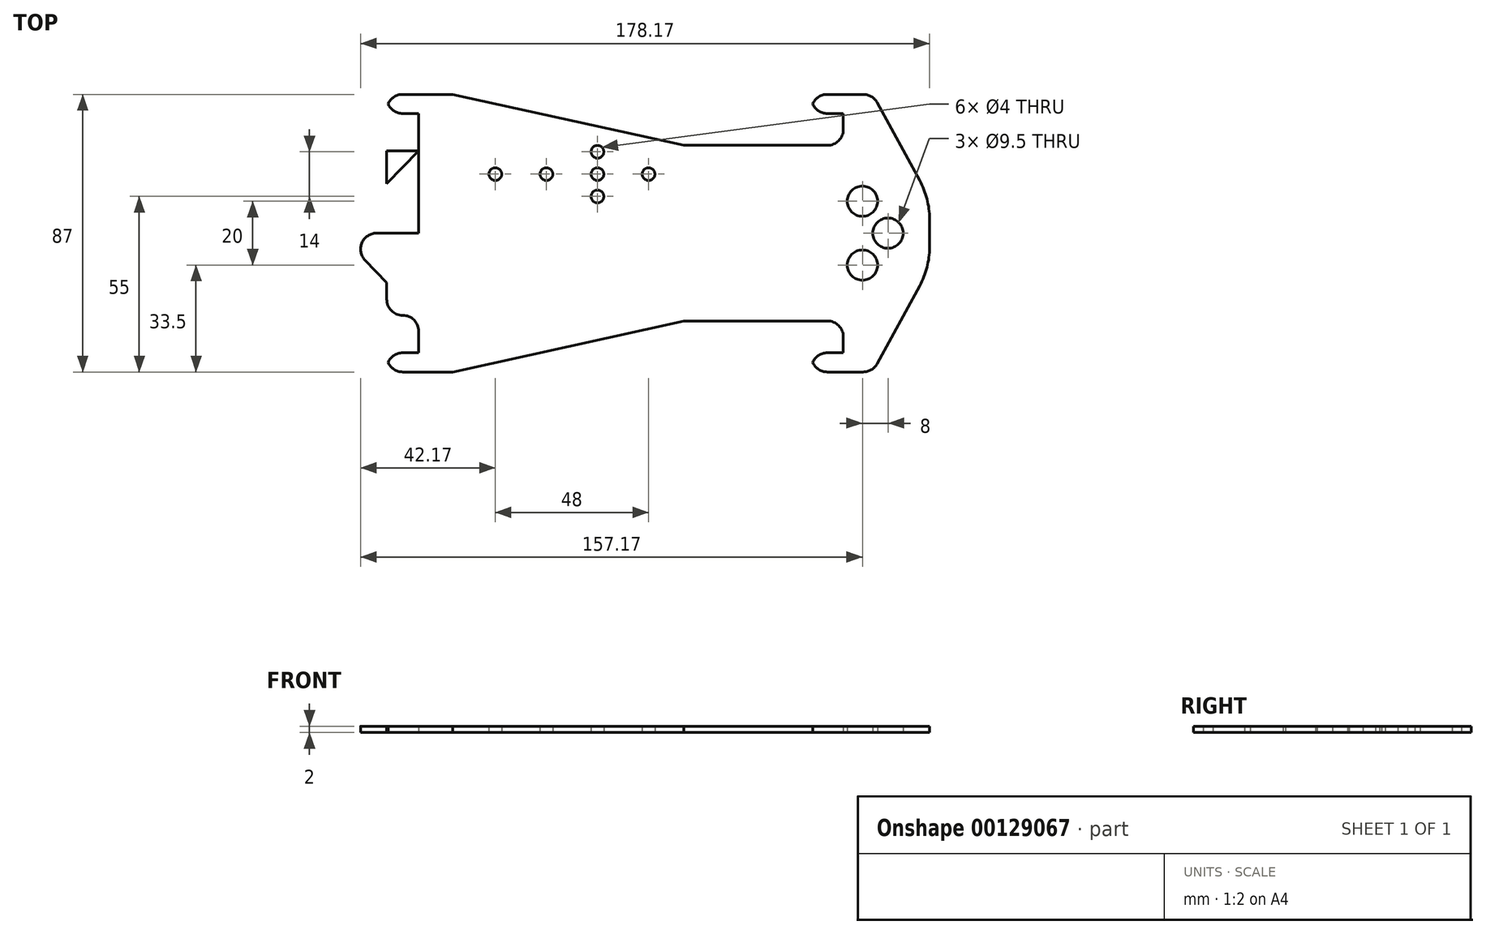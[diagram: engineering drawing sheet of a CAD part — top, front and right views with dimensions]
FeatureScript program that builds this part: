
annotation { "Feature Type Name" : "Feature", "Feature Type Description" : "" }
export const myFeature = defineFeature(function(context is Context, id is Id, definition is map)
    precondition{}
    {
        {
            var Q0;
            Q0=qCreatedBy(makeId("Top.planeOp"),FACE);
            var sketch = newSketch(context, id + "F0", { "sketchPlane" : qUnion([Q0])});
            skLineSegment(sketch, "E0.bottom", {"start": v(85, -43.5) * mm, "end": v(-85, -43.5) * mm});
            skLineSegment(sketch, "E0.top", {"start": v(85, 43.5) * mm, "end": v(-85, 43.5) * mm});
            skLineSegment(sketch, "E0.left", {"start": v(85, -43.5) * mm, "end": v(85, 43.5) * mm});
            skLineSegment(sketch, "E0.right", {"start": v(-85, -43.5) * mm, "end": v(-85, 43.5) * mm});
            skPoint(sketch, "E0.middle", {"position": v(0, 0) * mm});
            skLineSegment(sketch, "E1", {"start": v(-85, -37.5) * mm, "end": v(-75, -37.5) * mm});
            skLineSegment(sketch, "E2", {"start": v(-75, -37.5) * mm, "end": v(-75, 0) * mm});
            skLineSegment(sketch, "E3.MirrorCS", {"start": v(-75, 37.5) * mm, "end": v(-75, 0) * mm});
            skLineSegment(sketch, "E4.MirrorCS", {"start": v(-85, 37.5) * mm, "end": v(-75, 37.5) * mm});
            skLineSegment(sketch, "E5", {"start": v(48, -43.5) * mm, "end": v(48, -37.5) * mm});
            skLineSegment(sketch, "E6", {"start": v(48, -37.5) * mm, "end": v(58, -37.5) * mm});
            skLineSegment(sketch, "E7", {"start": v(58, -37.5) * mm, "end": v(58, -27.5) * mm});
            skLineSegment(sketch, "E8", {"start": v(58, -27.5) * mm, "end": v(8, -27.5) * mm});
            skLineSegment(sketch, "E9", {"start": v(8, -27.5) * mm, "end": v(-64.29, -43.5) * mm});
            skLineSegment(sketch, "E10.MirrorCS", {"start": v(8, 27.5) * mm, "end": v(-64.29, 43.5) * mm});
            skLineSegment(sketch, "E11.MirrorCS", {"start": v(58, 27.5) * mm, "end": v(8, 27.5) * mm});
            skLineSegment(sketch, "E12.MirrorCS", {"start": v(58, 37.5) * mm, "end": v(58, 27.5) * mm});
            skLineSegment(sketch, "E13.MirrorCS", {"start": v(48, 37.5) * mm, "end": v(58, 37.5) * mm});
            skLineSegment(sketch, "E14.MirrorCS", {"start": v(48, 43.5) * mm, "end": v(48, 37.5) * mm});
            skLineSegment(sketch, "E15", {"start": v(67.19, -43.5) * mm, "end": v(85, -10.86) * mm});
            skLineSegment(sketch, "E16.MirrorCS", {"start": v(67.19, 43.5) * mm, "end": v(85, 10.86) * mm});
            skCircle(sketch, "E17", {"center": v(-3, 18.5) * mm, "radius": 2 * mm});
            skCircle(sketch, "E18", {"center": v(-35, 18.5) * mm, "radius": 2 * mm});
            skCircle(sketch, "E19", {"center": v(-19, 11.5) * mm, "radius": 2 * mm});
            skCircle(sketch, "E20", {"center": v(-19, 25.5) * mm, "radius": 2 * mm});
            skCircle(sketch, "E21", {"center": v(-51, 18.5) * mm, "radius": 2 * mm});
            skLineSegment(sketch, "E22", {"start": v(-75, 25.74) * mm, "end": v(-100, 25.74) * mm});
            skLineSegment(sketch, "E23", {"start": v(-100, 25.74) * mm, "end": v(-100, 0) * mm});
            skLineSegment(sketch, "E24", {"start": v(-100, 0) * mm, "end": v(-75, 0) * mm});
            skLineSegment(sketch, "E25.MirrorCS", {"start": v(-75, -25.74) * mm, "end": v(-100, -25.74) * mm});
            skLineSegment(sketch, "E26.MirrorCS", {"start": v(-100, -25.74) * mm, "end": v(-100, 0) * mm});
            skCircle(sketch, "E27", {"center": v(72, 0) * mm, "radius": 4.75 * mm});
            skCircle(sketch, "E28", {"center": v(64, -10) * mm, "radius": 4.75 * mm});
            skCircle(sketch, "E29.MirrorC", {"center": v(64, 10) * mm, "radius": 4.75 * mm});
            skCircle(sketch, "E30", {"center": v(-19, 18.5) * mm, "radius": 2 * mm});
            skCircle(sketch, "E31", {"center": v(-87.5, 0) * mm, "radius": 4.75 * mm});
            skLineSegment(sketch, "E32", {"start": v(-75, 25.74) * mm, "end": v(-100, 0) * mm});
            skLineSegment(sketch, "E33", {"start": v(-75, -25.74) * mm, "end": v(-100, 0) * mm});
            skSolve(sketch);
        }
        {
            var Q0;
            {var subQ8=sQuery(id+"F0.wireOp",EDGE,"E1");Q0=makeQuery(id+"F0.imprint","IMPRINT",FACE,{"disambiguationData":[TD([[makeQuery(id+"F0.imprint","IMPRINT",EDGE,{"derivedFrom":subQ8}),-1.0]])]});}
            var Q1;
            {var subQ0=sQuery(id+"F0.wireOp",EDGE,"E31");var subQ1=sQuery(id+"F0.wireOp",EDGE,"E0.right");var subQ2=makeQuery(id+"F0.imprint","INTERSECT",VERTEX,{"disambiguationData":[OD(1.0)],"derivedFrom":[subQ1,subQ0]});Q1=makeQuery(id+"F0.imprint","IMPRINT",FACE,{"disambiguationData":[TD([[makeQuery(id+"F0.imprint","IMPRINT",EDGE,{"disambiguationData":[TD([[subQ2,-1.0]])],"derivedFrom":subQ1}),-1.0]])]});}
            var Q2;
            {var subQ0=sQuery(id+"F0.wireOp",EDGE,"E31");var subQ1=sQuery(id+"F0.wireOp",EDGE,"E0.right");var subQ2=makeQuery(id+"F0.imprint","INTERSECT",VERTEX,{"disambiguationData":[OD(1.0)],"derivedFrom":[subQ1,subQ0]});Q2=makeQuery(id+"F0.imprint","IMPRINT",FACE,{"disambiguationData":[TD([[makeQuery(id+"F0.imprint","IMPRINT",EDGE,{"disambiguationData":[TD([[subQ2,-1.0]])],"derivedFrom":subQ1}),1.0]])]});}
            var Q3;
            {var subQ1=sQuery(id+"F0.wireOp",EDGE,"E0.right");var subQ7=sQuery(id+"F0.wireOp",EDGE,"E33");var subQ9=makeQuery(id+"F0.imprint","INTERSECT",VERTEX,{"derivedFrom":[subQ1,subQ7]});Q3=makeQuery(id+"F0.imprint","IMPRINT",FACE,{"disambiguationData":[TD([[makeQuery(id+"F0.imprint","IMPRINT",EDGE,{"disambiguationData":[TD([[subQ9,-1.0]])],"derivedFrom":subQ1}),-1.0]])]});}
            var Q4;
            {var subQ0=sQuery(id+"F0.wireOp",EDGE,"E33");var subQ1=sQuery(id+"F0.wireOp",EDGE,"E0.right");var subQ2=makeQuery(id+"F0.imprint","INTERSECT",VERTEX,{"derivedFrom":[subQ1,subQ0]});Q4=makeQuery(id+"F0.imprint","IMPRINT",FACE,{"disambiguationData":[TD([[makeQuery(id+"F0.imprint","IMPRINT",EDGE,{"disambiguationData":[TD([[subQ2,-1.0]])],"derivedFrom":subQ1}),1.0]])]});}
            var Q5;
            {var subQ0=sQuery(id+"F0.wireOp",EDGE,"E22");var subQ1=sQuery(id+"F0.wireOp",EDGE,"E0.right");var subQ2=makeQuery(id+"F0.imprint","INTERSECT",VERTEX,{"derivedFrom":[subQ1,subQ0]});Q5=makeQuery(id+"F0.imprint","IMPRINT",FACE,{"disambiguationData":[TD([[makeQuery(id+"F0.imprint","IMPRINT",EDGE,{"disambiguationData":[TD([[subQ2,1.0]])],"derivedFrom":subQ1}),-1.0]])]});}
            var Q6;
            {var subQ0=sQuery(id+"F0.wireOp",EDGE,"E25.MirrorCS");var subQ1=sQuery(id+"F0.wireOp",EDGE,"E0.right");var subQ2=makeQuery(id+"F0.imprint","INTERSECT",VERTEX,{"derivedFrom":[subQ1,subQ0]});Q6=makeQuery(id+"F0.imprint","IMPRINT",FACE,{"disambiguationData":[TD([[makeQuery(id+"F0.imprint","IMPRINT",EDGE,{"disambiguationData":[TD([[subQ2,-1.0]])],"derivedFrom":subQ1}),-1.0]])]});}
            extrude(context, id + "F1", {"entities" : qUnion([Q0, Q1, Q2, Q3, Q4, Q5, Q6]), "depth" : 2 * mm});
        }
        {
            var Q0;
            Q0=makeQuery(id+"F1.opExtrude","SWEPT_EDGE",EDGE,{"disambiguationData":[OSD([sQuery(id+"F0.wireOp",EDGE,"E0.top"),sQuery(id+"F0.wireOp",EDGE,"E16.MirrorCS")])]});
            var Q1;
            Q1=makeQuery(id+"F1.opExtrude","SWEPT_EDGE",EDGE,{"disambiguationData":[OSD([sQuery(id+"F0.wireOp",EDGE,"E0.top"),sQuery(id+"F0.wireOp",EDGE,"E14.MirrorCS")])]});
            var Q2;
            Q2=makeQuery(id+"F1.opExtrude","SWEPT_EDGE",EDGE,{"disambiguationData":[OSD([sQuery(id+"F0.wireOp",EDGE,"E0.bottom"),sQuery(id+"F0.wireOp",EDGE,"E0.right")])]});
            var Q3;
            Q3=makeQuery(id+"F1.opExtrude","SWEPT_EDGE",EDGE,{"disambiguationData":[OSD([sQuery(id+"F0.wireOp",EDGE,"E0.right"),sQuery(id+"F0.wireOp",EDGE,"E1")])]});
            var Q4;
            Q4=makeQuery(id+"F1.opExtrude","SWEPT_EDGE",EDGE,{"disambiguationData":[OSD([sQuery(id+"F0.wireOp",EDGE,"E0.bottom"),sQuery(id+"F0.wireOp",EDGE,"E5")])]});
            var Q5;
            Q5=makeQuery(id+"F1.opExtrude","SWEPT_EDGE",EDGE,{"disambiguationData":[OSD([sQuery(id+"F0.wireOp",EDGE,"E5"),sQuery(id+"F0.wireOp",EDGE,"E6")])]});
            var Q6;
            Q6=makeQuery(id+"F1.opExtrude","SWEPT_EDGE",EDGE,{"disambiguationData":[OSD([sQuery(id+"F0.wireOp",EDGE,"E13.MirrorCS"),sQuery(id+"F0.wireOp",EDGE,"E14.MirrorCS")])]});
            var Q7;
            Q7=makeQuery(id+"F1.opExtrude","SWEPT_EDGE",EDGE,{"disambiguationData":[OSD([sQuery(id+"F0.wireOp",EDGE,"E0.right"),sQuery(id+"F0.wireOp",EDGE,"E4.MirrorCS")])]});
            var Q8;
            Q8=makeQuery(id+"F1.opExtrude","SWEPT_EDGE",EDGE,{"disambiguationData":[OSD([sQuery(id+"F0.wireOp",EDGE,"E0.top"),sQuery(id+"F0.wireOp",EDGE,"E0.right")])]});
            var Q9;
            Q9=makeQuery(id+"F1.opExtrude","SWEPT_EDGE",EDGE,{"disambiguationData":[OSD([sQuery(id+"F0.wireOp",EDGE,"E0.bottom"),sQuery(id+"F0.wireOp",EDGE,"E15")])]});
            fillet(context, id + "F2", {"entities" : qUnion([Q0, Q1, Q2, Q3, Q4, Q5, Q6, Q7, Q8, Q9]), "radius" : 5 * mm, "tangentPropagation" : true, "allowEdgeOverflow" : false});
        }
        {
            var Q0;
            Q0=makeQuery(id+"F1.opExtrude","SWEPT_EDGE",EDGE,{"disambiguationData":[OSD([sQuery(id+"F0.wireOp",EDGE,"E7"),sQuery(id+"F0.wireOp",EDGE,"E8")])]});
            var Q1;
            Q1=makeQuery(id+"F1.opExtrude","SWEPT_EDGE",EDGE,{"disambiguationData":[OSD([sQuery(id+"F0.wireOp",EDGE,"E11.MirrorCS"),sQuery(id+"F0.wireOp",EDGE,"E12.MirrorCS")])]});
            fillet(context, id + "F3", {"entities" : qUnion([Q0, Q1]), "radius" : 5 * mm, "tangentPropagation" : true, "allowEdgeOverflow" : false});
        }
        {
            var Q0;
            Q0=makeQuery(id+"F1.opExtrude","SWEPT_EDGE",EDGE,{"disambiguationData":[OSD([sQuery(id+"F0.wireOp",EDGE,"E22"),sQuery(id+"F0.wireOp",EDGE,"E23")])]});
            var Q1;
            Q1=makeQuery(id+"F1.opExtrude","SWEPT_EDGE",EDGE,{"disambiguationData":[OSD([sQuery(id+"F0.wireOp",EDGE,"E25.MirrorCS"),sQuery(id+"F0.wireOp",EDGE,"E26.MirrorCS")])]});
            var Q2;
            Q2=makeQuery(id+"F1.opExtrude","SWEPT_EDGE",EDGE,{"disambiguationData":[OSD([sQuery(id+"F0.wireOp",EDGE,"E3.MirrorCS"),sQuery(id+"F0.wireOp",EDGE,"E22")])]});
            var Q3;
            Q3=makeQuery(id+"F1.opExtrude","SWEPT_EDGE",EDGE,{"disambiguationData":[OSD([sQuery(id+"F0.wireOp",EDGE,"E2"),sQuery(id+"F0.wireOp",EDGE,"E25.MirrorCS")])]});
            var Q4;
            Q4=makeQuery(id+"F1.opExtrude","SWEPT_EDGE",EDGE,{"disambiguationData":[OSD([sQuery(id+"F0.wireOp",EDGE,"E23"),sQuery(id+"F0.wireOp",EDGE,"E24"),sQuery(id+"F0.wireOp",EDGE,"E26.MirrorCS"),sQuery(id+"F0.wireOp",EDGE,"E32"),sQuery(id+"F0.wireOp",EDGE,"E33")])]});
            fillet(context, id + "F4", {"entities" : qUnion([Q0, Q1, Q2, Q3, Q4]), "radius" : 5 * mm, "tangentPropagation" : true, "allowEdgeOverflow" : false});
        }
        {
            var Q0;
            Q0=makeQuery(id+"F1.opExtrude","SWEPT_EDGE",EDGE,{"disambiguationData":[OSD([sQuery(id+"F0.wireOp",EDGE,"E0.left"),sQuery(id+"F0.wireOp",EDGE,"E15")])]});
            var Q1;
            Q1=makeQuery(id+"F1.opExtrude","SWEPT_EDGE",EDGE,{"disambiguationData":[OSD([sQuery(id+"F0.wireOp",EDGE,"E0.left"),sQuery(id+"F0.wireOp",EDGE,"E16.MirrorCS")])]});
            fillet(context, id + "F5", {"entities" : qUnion([Q0, Q1]), "radius" : 25 * mm, "tangentPropagation" : true, "allowEdgeOverflow" : false});
        }
    });
